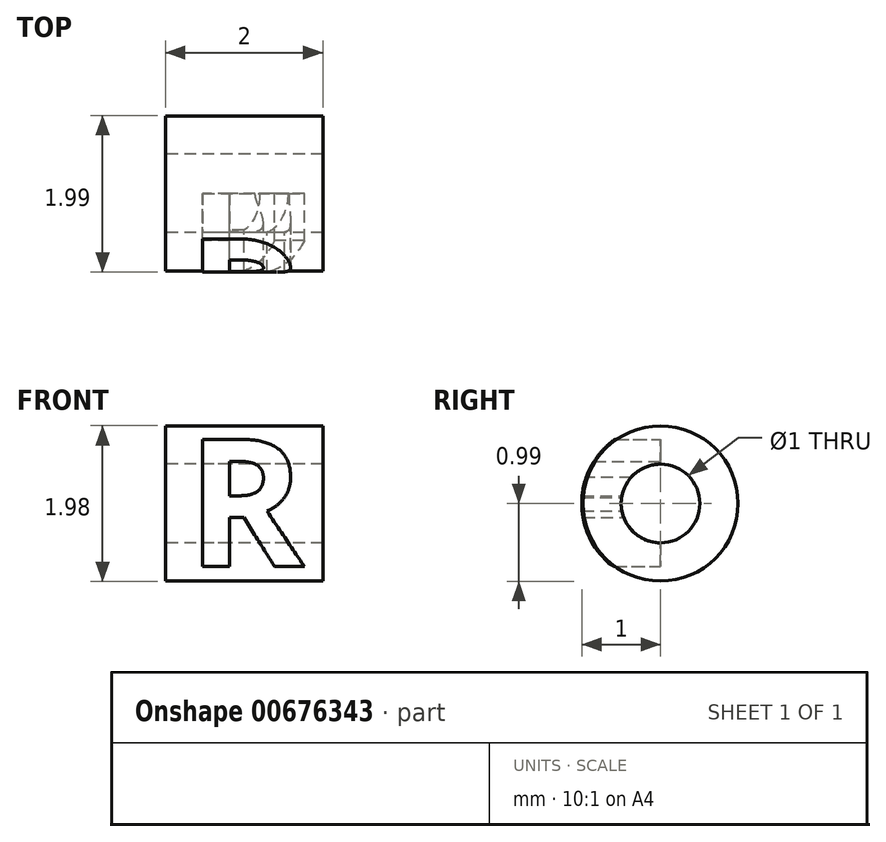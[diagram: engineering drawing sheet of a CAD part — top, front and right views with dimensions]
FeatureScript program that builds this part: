
annotation { "Feature Type Name" : "Feature", "Feature Type Description" : "" }
export const myFeature = defineFeature(function(context is Context, id is Id, definition is map)
    precondition{}
    {
        {
            var Q0;
            Q0=qCreatedBy(makeId("Right.planeOp"),FACE);
            var sketch = newSketch(context, id + "F0", { "sketchPlane" : qUnion([Q0])});
            skCircle(sketch, "E0", {"center": v(0, 0) * mm, "radius": 0.5 * mm});
            skCircle(sketch, "E1", {"center": v(0, 0) * mm, "radius": 1 * mm});
            skCircle(sketch, "E2", {"center": v(0, 0) * mm, "radius": 0.98 * mm});
            skSolve(sketch);
        }
        {
            var Q0;
            Q0=makeQuery(id+"F0.imprint","IMPRINT",FACE,{"disambiguationData":[TD([[makeQuery(id+"F0.imprint","IMPRINT",EDGE,{"derivedFrom":sQuery(id+"F0.wireOp",EDGE,"E0")}),-1.0]])]});
            var Q1;
            Q1=makeQuery(id+"F0.imprint","IMPRINT",FACE,{"disambiguationData":[TD([[makeQuery(id+"F0.imprint","IMPRINT",EDGE,{"derivedFrom":sQuery(id+"F0.wireOp",EDGE,"E1")}),1.0]])]});
            extrude(context, id + "F1", {"entities" : qUnion([Q0, Q1]), "depth" : 2 * mm, "offsetDistance" : 25 * mm});
        }
        {
            var Q0;
            Q0=qCreatedBy(makeId("Front.planeOp"),FACE);
            var sketch = newSketch(context, id + "F2", { "sketchPlane" : qUnion([Q0])});
            skText(sketch, "E3", { "text": "R", "fontName": "OpenSans-Bold.ttf"});
            const initialGuessF2  = {"E3": [0.00027, -0.0008, 1, 0, 0.00163]};
            skSetInitialGuess(sketch, initialGuessF2);
            skSolve(sketch);
        }
        {
            var Q0;
            Q0=qSketchRegion(id+"F2",true);
            var Q1;
            Q1=qConstructionFilter(qBodyType(qCreatedBy(id+"F2",EDGE),BodyType.WIRE),ConstructionObject.NO);
            var Q2;
            Q2=makeQuery(id+"F1.opExtrude","SWEPT_FACE",FACE,{"disambiguationData":[OSD([sQuery(id+"F0.wireOp",EDGE,"E1")])]});
            var Q3;
            Q3=makeQuery(id+"F1.opExtrude","SWEPT_BODY",BODY,{"disambiguationData":[OSD([sQuery(id+"F0.wireOp",EDGE,"E0"),sQuery(id+"F0.wireOp",EDGE,"E1")])]});
            var Q4;
            Q4=sQuery(id+"F0.wireOp",VERTEX,"27635d6e-dcd6-4653-b727-4819003c0945");
            extrude(context, id + "F3", {"entities" : qUnion([Q0]), "operationType" : NewBodyOperationType.INTERSECT, "surfaceEntities" : qUnion([Q1]), "endBound" : BoundingType.UP_TO_SURFACE, "endBoundEntityFace" : qUnion([Q2]), "endBoundEntityBody" : qUnion([Q3]), "endBoundEntityVertex" : qUnion([Q4]), "depth" : 25 * mm, "offsetDistance" : 25 * mm});
        }
        {
            var Q0;
            Q0=makeQuery(id+"F0.imprint","IMPRINT",FACE,{"disambiguationData":[TD([[makeQuery(id+"F0.imprint","IMPRINT",EDGE,{"derivedFrom":sQuery(id+"F0.wireOp",EDGE,"E0")}),-1.0]])]});
            extrude(context, id + "F4", {"entities" : qUnion([Q0]), "depth" : 2 * mm, "offsetDistance" : 25 * mm});
        }
    });
